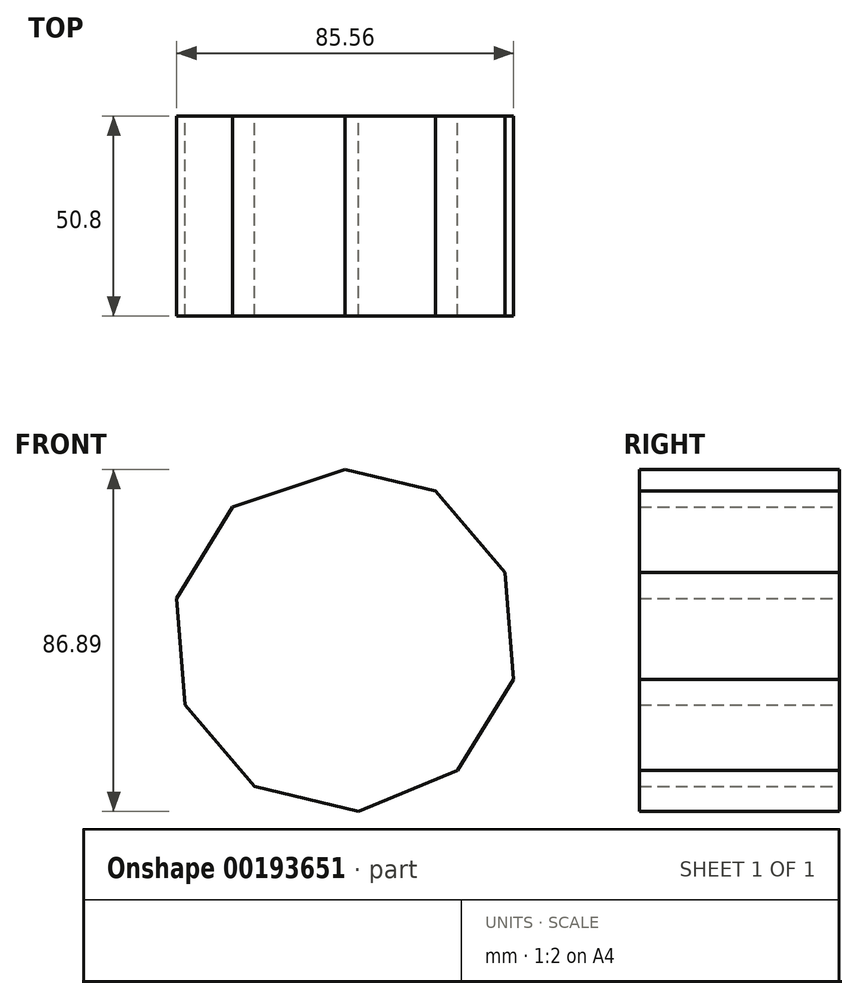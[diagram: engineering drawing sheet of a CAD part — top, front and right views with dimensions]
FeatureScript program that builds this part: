
annotation { "Feature Type Name" : "Feature", "Feature Type Description" : "" }
export const myFeature = defineFeature(function(context is Context, id is Id, definition is map)
    precondition{}
    {
        {
            var Q0;
            Q0=qCreatedBy(makeId("Front.planeOp"),FACE);
            var sketch = newSketch(context, id + "F0", { "sketchPlane" : qUnion([Q0])});
            skLineSegment(sketch, "E0.0", {"start": v(-22.98, -37.51) * mm, "end": v(-40.64, -16.84) * mm});
            skLineSegment(sketch, "E0.1", {"start": v(-40.64, -16.84) * mm, "end": v(-42.78, 10.27) * mm});
            skLineSegment(sketch, "E0.2", {"start": v(-42.78, 10.27) * mm, "end": v(-28.57, 33.45) * mm});
            skLineSegment(sketch, "E0.3", {"start": v(-28.57, 33.45) * mm, "end": v(0, 43.03) * mm});
            skLineSegment(sketch, "E0.4", {"start": v(0, 43.03) * mm, "end": v(22.98, 37.51) * mm});
            skLineSegment(sketch, "E0.5", {"start": v(22.98, 37.51) * mm, "end": v(40.64, 16.84) * mm});
            skLineSegment(sketch, "E0.6", {"start": v(40.64, 16.84) * mm, "end": v(42.78, -10.27) * mm});
            skLineSegment(sketch, "E0.7", {"start": v(42.78, -10.27) * mm, "end": v(28.57, -33.45) * mm});
            skLineSegment(sketch, "E0.8", {"start": v(28.57, -33.45) * mm, "end": v(3.45, -43.86) * mm});
            skLineSegment(sketch, "E0.9", {"start": v(3.45, -43.86) * mm, "end": v(-22.98, -37.51) * mm});
            skPoint(sketch, "E0.0.midPoint", {"position": v(-31.81, -27.17) * mm});
            skLineSegment(sketch, "E1", {"start": v(-28.57, 33.45) * mm, "end": v(0, 0) * mm});
            skLineSegment(sketch, "E2", {"start": v(0, 43.03) * mm, "end": v(0, 0) * mm});
            skLineSegment(sketch, "E3", {"start": v(22.98, 37.51) * mm, "end": v(0, 0) * mm});
            skLineSegment(sketch, "E4", {"start": v(40.64, 16.84) * mm, "end": v(0, 0) * mm});
            skLineSegment(sketch, "E5", {"start": v(42.78, -10.27) * mm, "end": v(0, 0) * mm});
            skLineSegment(sketch, "E6", {"start": v(28.57, -33.45) * mm, "end": v(0, 0) * mm});
            skLineSegment(sketch, "E7", {"start": v(3.45, -43.86) * mm, "end": v(0, 0) * mm});
            skLineSegment(sketch, "E8", {"start": v(-22.98, -37.51) * mm, "end": v(0, 0) * mm});
            skLineSegment(sketch, "E9", {"start": v(-40.64, -16.84) * mm, "end": v(0, 0) * mm});
            skLineSegment(sketch, "E10", {"start": v(-42.78, 10.27) * mm, "end": v(0, 0) * mm});
            skSolve(sketch);
        }
        {
            var Q0;
            Q0=makeQuery(id+"F0.imprint","IMPRINT",FACE,{"disambiguationData":[TD([[makeQuery(id+"F0.imprint","IMPRINT",EDGE,{"derivedFrom":sQuery(id+"F0.wireOp",EDGE,"E0.3")}),-1.0]])]});
            var Q1;
            Q1=makeQuery(id+"F0.imprint","IMPRINT",FACE,{"disambiguationData":[TD([[makeQuery(id+"F0.imprint","IMPRINT",EDGE,{"derivedFrom":sQuery(id+"F0.wireOp",EDGE,"E0.5")}),-1.0]])]});
            var Q2;
            Q2=makeQuery(id+"F0.imprint","IMPRINT",FACE,{"disambiguationData":[TD([[makeQuery(id+"F0.imprint","IMPRINT",EDGE,{"derivedFrom":sQuery(id+"F0.wireOp",EDGE,"E0.7")}),-1.0]])]});
            var Q3;
            Q3=makeQuery(id+"F0.imprint","IMPRINT",FACE,{"disambiguationData":[TD([[makeQuery(id+"F0.imprint","IMPRINT",EDGE,{"derivedFrom":sQuery(id+"F0.wireOp",EDGE,"E0.9")}),-1.0]])]});
            var Q4;
            Q4=makeQuery(id+"F0.imprint","IMPRINT",FACE,{"disambiguationData":[TD([[makeQuery(id+"F0.imprint","IMPRINT",EDGE,{"derivedFrom":sQuery(id+"F0.wireOp",EDGE,"E0.1")}),-1.0]])]});
            var Q5;
            Q5=makeQuery(id+"F0.imprint","IMPRINT",FACE,{"disambiguationData":[TD([[makeQuery(id+"F0.imprint","IMPRINT",EDGE,{"derivedFrom":sQuery(id+"F0.wireOp",EDGE,"E0.2")}),-1.0]])]});
            var Q6;
            Q6=makeQuery(id+"F0.imprint","IMPRINT",FACE,{"disambiguationData":[TD([[makeQuery(id+"F0.imprint","IMPRINT",EDGE,{"derivedFrom":sQuery(id+"F0.wireOp",EDGE,"E0.4")}),-1.0]])]});
            var Q7;
            Q7=makeQuery(id+"F0.imprint","IMPRINT",FACE,{"disambiguationData":[TD([[makeQuery(id+"F0.imprint","IMPRINT",EDGE,{"derivedFrom":sQuery(id+"F0.wireOp",EDGE,"E0.6")}),-1.0]])]});
            var Q8;
            Q8=makeQuery(id+"F0.imprint","IMPRINT",FACE,{"disambiguationData":[TD([[makeQuery(id+"F0.imprint","IMPRINT",EDGE,{"derivedFrom":sQuery(id+"F0.wireOp",EDGE,"E0.8")}),-1.0]])]});
            var Q9;
            Q9=makeQuery(id+"F0.imprint","IMPRINT",FACE,{"disambiguationData":[TD([[makeQuery(id+"F0.imprint","IMPRINT",EDGE,{"derivedFrom":sQuery(id+"F0.wireOp",EDGE,"E0.0")}),-1.0]])]});
            extrude(context, id + "F1", {"entities" : qUnion([Q0, Q1, Q2, Q3, Q4, Q5, Q6, Q7, Q8, Q9]), "endBound" : BoundingType.SYMMETRIC, "depth" : 50.8 * mm});
        }
    });
